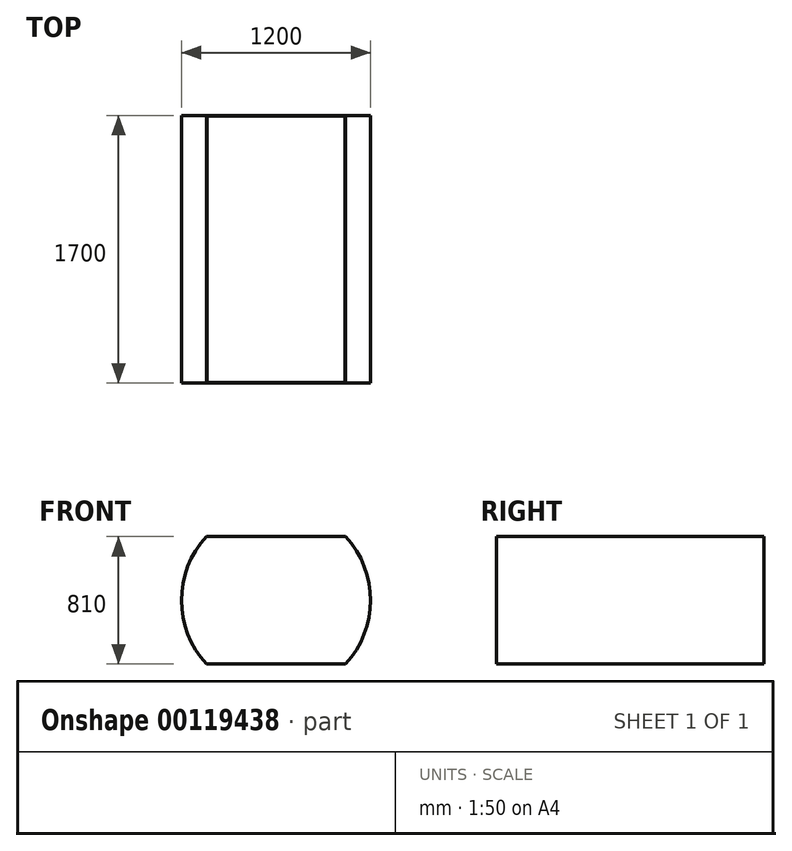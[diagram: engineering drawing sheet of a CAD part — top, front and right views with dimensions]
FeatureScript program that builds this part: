
annotation { "Feature Type Name" : "Feature", "Feature Type Description" : "" }
export const myFeature = defineFeature(function(context is Context, id is Id, definition is map)
    precondition{}
    {
        {
            var Q0;
            Q0=qCreatedBy(makeId("Front.planeOp"),FACE);
            var sketch = newSketch(context, id + "F0", { "sketchPlane" : qUnion([Q0])});
            skArc(sketch, "E0", {"start": v(-442.7, 405) * mm, "mid": v(-600, 0) * mm, "end": v(-442.7, -405) * mm});
            skLineSegment(sketch, "E1", {"start": v(-787.44, 0) * mm, "end": v(769.65, 0) * mm, "construction": true});
            skLineSegment(sketch, "E2", {"start": v(-787.44, 405) * mm, "end": v(769.65, 405) * mm, "construction": true});
            skLineSegment(sketch, "E3.MirrorCS", {"start": v(-787.44, -405) * mm, "end": v(769.65, -405) * mm, "construction": true});
            skArc(sketch, "E4.trimOffspring", {"start": v(442.7, -405) * mm, "mid": v(600, 0) * mm, "end": v(442.7, 405) * mm});
            skLineSegment(sketch, "E5", {"start": v(-442.7, 405) * mm, "end": v(442.7, 405) * mm});
            skLineSegment(sketch, "E6", {"start": v(-442.7, -405) * mm, "end": v(442.7, -405) * mm});
            skSolve(sketch);
        }
        {
            var Q0;
            Q0 = qSketchRegion(id + "F0", true);
            extrude(context, id + "F1", {"entities" : qUnion([Q0]), "oppositeDirection" : true, "depth" : 1700 * mm});
        }
        {
            var Q0;
            Q0=makeQuery(id+"F1.opExtrude","SWEPT_FACE",FACE,{"disambiguationData":[OSD([sQuery(id+"F0.wireOp",EDGE,"E5")])]});
            shell(context, id + "F2", {"entities" : qUnion([Q0]), "thickness" : 2.5 * mm});
        }
    });
